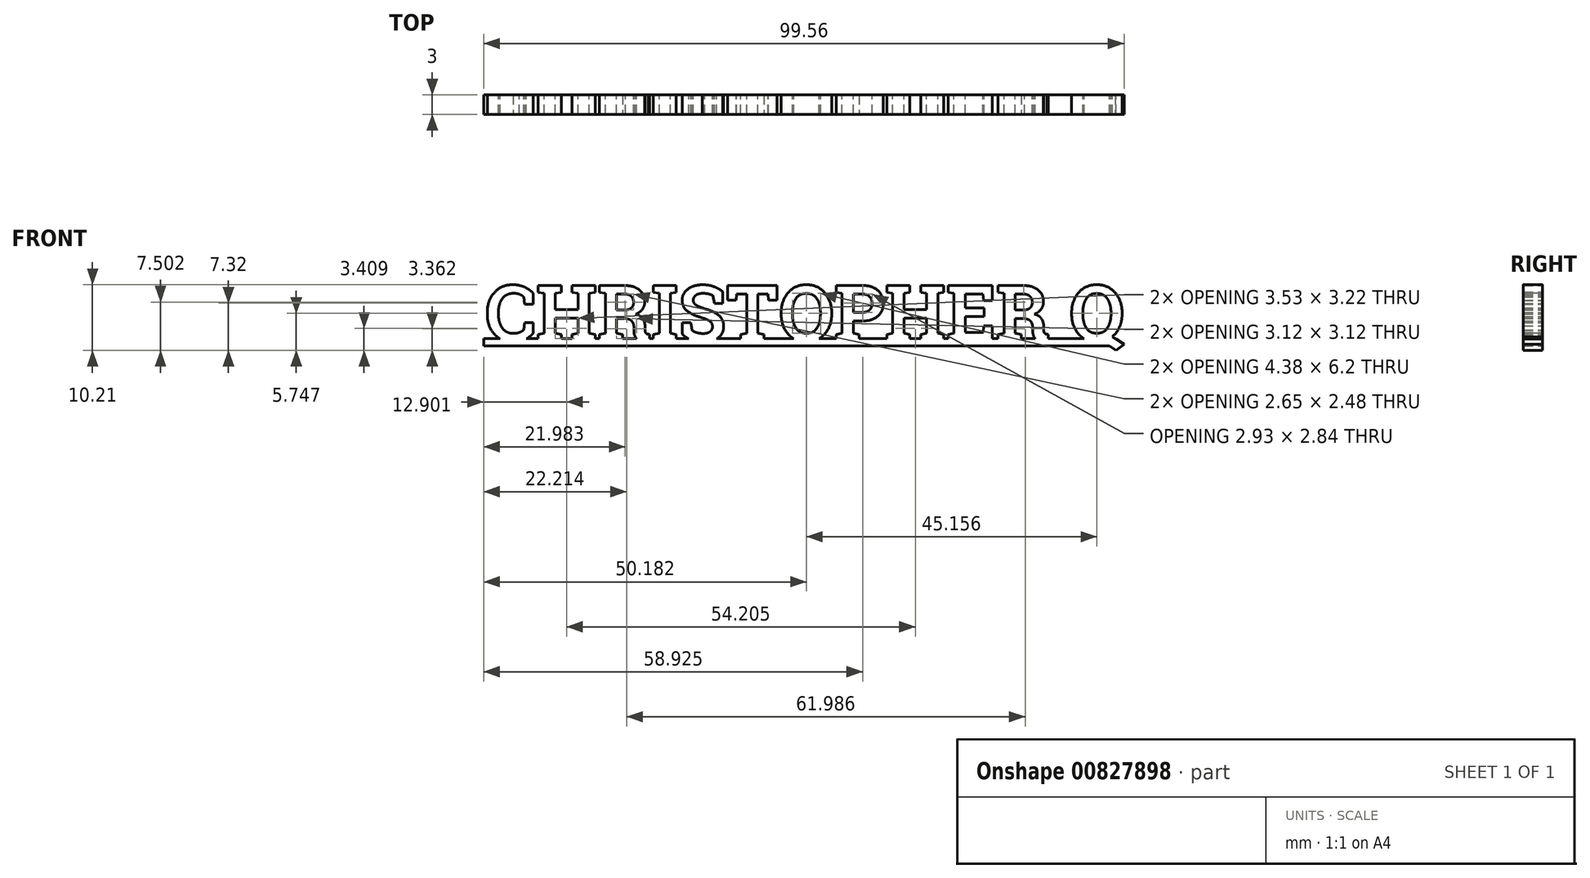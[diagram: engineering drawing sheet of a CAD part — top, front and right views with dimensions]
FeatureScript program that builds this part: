
annotation { "Feature Type Name" : "Feature", "Feature Type Description" : "" }
export const myFeature = defineFeature(function(context is Context, id is Id, definition is map)
    precondition{}
    {
        {
            var Q0;
            Q0=qCreatedBy(makeId("Front.planeOp"),FACE);
            var sketch = newSketch(context, id + "F0", { "sketchPlane" : qUnion([Q0])});
            skText(sketch, "E0", { "text": "CHRISTOPHER Q", "fontName": "RobotoSlab-Bold.ttf"});
            const initialGuessF0  = {"E0": [-0.0498, -0.00038, 1, 0, 0.00877]};
            skSetInitialGuess(sketch, initialGuessF0);
            skSolve(sketch);
        }
        {
            var Q0;
            Q0=qCreatedBy(makeId("Front.planeOp"),FACE);
            var sketch = newSketch(context, id + "F1", { "sketchPlane" : qUnion([Q0])});
            skLineSegment(sketch, "E1.bottom", {"start": v(-50.05, 0) * mm, "end": v(48.24, 0) * mm});
            skLineSegment(sketch, "E1.top", {"start": v(-50.05, -1.11) * mm, "end": v(48.24, -1.11) * mm});
            skLineSegment(sketch, "E1.left", {"start": v(-50.05, 0) * mm, "end": v(-50.05, -1.11) * mm});
            skLineSegment(sketch, "E1.right", {"start": v(48.24, 0) * mm, "end": v(48.24, -1.11) * mm});
            skSolve(sketch);
        }
        {
            var Q0;
            Q0 = qSketchRegion(id + "F0", true);
            extrude(context, id + "F2", {"entities" : qUnion([Q0]), "depth" : 3 * mm, "offsetDistance" : 25.4 * mm});
        }
        {
            var Q0;
            Q0 = qSketchRegion(id + "F1", true);
            extrude(context, id + "F3", {"entities" : qUnion([Q0]), "operationType" : NewBodyOperationType.ADD, "depth" : 3 * mm, "offsetDistance" : 25.4 * mm});
        }
    });
